# Revit family: Seating-Casual-Naughtone-Rhyme_Bench
name_source: partatom
category: Furniture
revit_build: Autodesk Revit 2015 (Build: 20150704_0715(x64)
units: mm (PartAtom-declared; Revit-internal decimal feet)

## types (1)
- RYM-BEN
    AdditionalMaterials = Additional material and finish options available. Please contact Naughtone direct for further information.
    Assembly Code = E2020
    AssetIdentifier = RYM-BEN
    AssetType = Movable
    BIMObjectName = Seating-Casual-Naughtone-Rhyme_Bench
    BarCode = 0.000000
    Category = 40.50.12 : Chairs, Seats and Benches
    CodePerformance = FISP Certified; ISO14001 Certified
    Color = Blue
    ComponentDescription = A landscape to approach from all angles, Rhyme is a modular seating system that can be used as a simple island or used to create ad-hoc zones within a space.
    Constituents = Wood Frame; Fabric; Steel fascia
    Cost = 0 $
    Description = Rhyme Bench
    DurationUnit = Years
    ExpectedLife = 15-20
    Finish = Polyster powder coat; various fabric finishes available
    Keynote = 40.50.12
    Manufacturer = Naughtone
    ManufacturerAddressUK = 201 Pannal Business Park, Station Road, Harrogate, HG3 1JL
    Material = FSC birch plywood frame; upholstered with CMHR foams
    Model = RYM-BEN
    ModelNumber = RYM-BEN
    ModelReference = Rhyme Bench
    NBSReference = 40.50.12
    Name = 1400mmx1400mmx420mm, Rhyme Bench
    NominalHeight = 420 mm  [stored 1.37795 ft]
    NominalLength = 1400 mm  [stored 4.59318 ft]
    NominalWidth = 1400 mm  [stored 4.59318 ft]
    Product URL = http://www.naughtone.com
    ProductInformation = http://www.naughtone.com
    ReplacementCost = 0.00
    SeatHeight = 420 mm  [stored 1.37795 ft]
    SerialNumber = 0.000000
    Shape = Rectangular
    Size = 1400mmx1400mmx420mm
    SustainabilityPerformance = 82.1% reusable content
    TagNumber = 0.000000
    Type Comments = 1400x1400x420
    TypeName = Seating-Casual-Naughtone-Rhyme_Bench
    URL = http://www.naughtone.com
    Uniclass2015 = 40.50.12
    Version = 1
    WarrantyDescription = 5 year warranty
    WarrantyDurationLabor = 5
    WarrantyDurationParts = 5
    WarrantyDurationUnit = Years
    _BIMspec_GUID = 0
    _current revision = 1
    _distributed by = www.bimbox.co.uk

note: [stored X ft] marks values corroborated as IEEE doubles in the binary element streams (Revit-internal decimal feet)

## geometry (parser evidence)
native form markers: Sweep x2
no freeform markers — native parametric forms only
